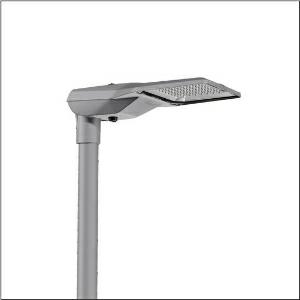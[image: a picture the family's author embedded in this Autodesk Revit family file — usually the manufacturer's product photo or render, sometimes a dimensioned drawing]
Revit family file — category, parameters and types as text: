
# Revit family: streetlight_sl_21_midi___p0_5a_5xe3v33t08nb_a5b7
name_source: partatom
category: Lighting Fixtures
units: mm (PartAtom-declared; Revit-internal decimal feet)

## family parameters
Cut with Voids When Loaded = No
Host = Face
Light Source = No
Part Type = Normal
Room Calculation Point = No
Round Connector Dimension = Use Diameter
Shared = No

## types (1)
- --- (1 x LED, 22310 lm, 151.2 W, 3000K)
    Apparent Load = 151 VA
    CIE Flux Codes = 37 73 96 100 100
    Color Rendering = 70
    Color Temperature = 3000K
    Default Elevation = 1800 mm
    Description = Streetlight SL 21 midi, mast luminaire, primary light control with lens, of PMMA, primary optical cover: cover, of toughened safety glass, transparent, light distribution: P0.5a, light emission: direct distribution, primary light characteristic: asymmetric, installation type: post-top, side-entry, LED, High Power LED, rated luminous flux: 22.310lm, luminous efficacy: 148lm/W, light colour: 730, colour temperature: 3000K, control gear: D4i, control: overheat protection, constant luminous flux control, time-dependent luminous flux control, flexible luminous flux parameterisation, pre-setting: logarithmic dimming characteristic, mains connection: 230..240V, AC, 50/60Hz, start of lifetime: 151W, end of service life: 157W, reduction: 70W, luminaire housing, of diecast aluminium, powder-coated, SITECO metallic grey (DB 702S), corrosivity category C5 high according to DIN EN ISO 12944, multi-level sealing system, sealing non-destructively replaceable, inclination adjustable: 0°, 5°, 10°, 15°, please order mast flange separately, length: 644mm, width: 335mm, height: 110mm, mast flange for spigot size: 42mm (side-entry): 5XC10008XM4, 60/48mm (side-entry/post-top): 5XC10108XM2, 76/60mm (side-entry/post-top): 5XC10108XM1, mounting height: 4..8m, Smart Interface below and above, protection rating (complete): IP66, insulation class (complete): insulation class II (safety insulation), certification: CE, ENEC, ENEC+, VDE, impact resistance: IK10, permissible operating ambient temperature for outdoor applications: -40..+50°C, standard-compliant lighting for roads and squares, packaging unit: 1 piece

Light Distribution: P0.5a
    Height = 111 mm
    Lamp = 1 x LED
    Lamp Light Flux = 22310 lm
    Lamp Power = 151.2 W
    Lamp count = 1
    Length = 644 mm
    Luminous efficacy = 148 lm/W
    Manufacturer = Siteco
    ModVariant = No
    Model = 5XE3V33T08NB
    Number of Poles = 1
    OnlyDefault = Yes
    Power Factor = 1
    Product Name = Streetlight SL 21 midi | P0.5a
    Product group = mast luminaire | pylon top
    ProductGroupID = 6100
    Protection Class = Protection class II
    Protection Degree = IP 66
    RLX_Detail_Level = 1
    RLX_Emergency_Light_Flux = 0 lm
    RLX_Emergency_Type = 0
    RLX_Emergency_Type_DB = No
    RlxData = <blob elided: 90801 chars, md5=6c325924>
    Socket = socket
    Standby Power = 0 W
    System Light Flux = 22310 lm
    System Power = 151 W
    Type Comments = factory setting: luminous flux: 100 % | dim-lin: 254 | 802 mA
    Type Image = l_1004304.jpg
    URL = http://relux.com
    VarID = @adj_076745
    Voltage = 0 V
    Weight = 0.00 kg
    Width = 336 mm

## geometry (parser evidence)
native form markers: Blend x4, Sweep x11
no freeform markers — native parametric forms only
